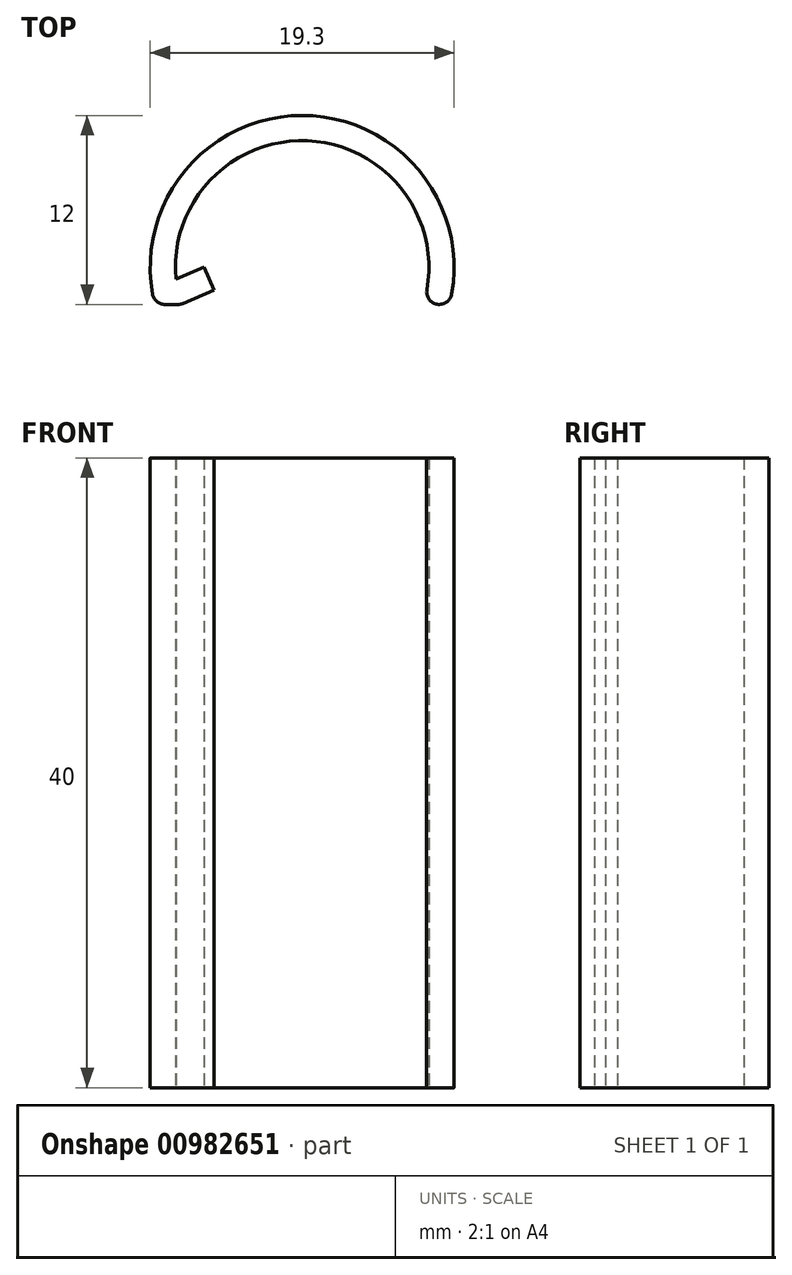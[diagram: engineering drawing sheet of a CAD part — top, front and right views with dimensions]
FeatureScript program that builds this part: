
annotation { "Feature Type Name" : "Feature", "Feature Type Description" : "" }
export const myFeature = defineFeature(function(context is Context, id is Id, definition is map)
    precondition{}
    {
        {
            var Q0;
            Q0=qCreatedBy(makeId("Top.planeOp"),FACE);
            var sketch = newSketch(context, id + "F0", { "sketchPlane" : qUnion([Q0])});
            skArc(sketch, "E0", {"start": v(7.7, -2.35) * mm, "mid": v(0.82, 8) * mm, "end": v(-8.02, -0.74) * mm});
            skArc(sketch, "E1.0", {"start": v(9.36, -2.35) * mm, "mid": v(0, 9.65) * mm, "end": v(-9.36, -2.35) * mm});
            skLineSegment(sketch, "E2", {"start": v(-6.2, 9.65) * mm, "end": v(12.66, 9.65) * mm, "construction": true});
            skArc(sketch, "E3.0", {"start": v(1.8, -0.14) * mm, "mid": v(0, 1.8) * mm, "end": v(-1.8, -0.14) * mm, "construction": true});
            skLineSegment(sketch, "E4", {"start": v(-7.7, -2.35) * mm, "end": v(-5.6, -1.44) * mm});
            skLineSegment(sketch, "E5.0", {"start": v(-8.02, -0.74) * mm, "end": v(-6.23, 0.03) * mm});
            skLineSegment(sketch, "E6.0", {"start": v(-9.36, -2.35) * mm, "end": v(-7.7, -2.35) * mm});
            skLineSegment(sketch, "E7.trimOffspring", {"start": v(7.7, -2.35) * mm, "end": v(9.36, -2.35) * mm});
            skLineSegment(sketch, "E8.0", {"start": v(-9.08, -2.95) * mm, "end": v(-9.72, -1.48) * mm, "construction": true});
            skLineSegment(sketch, "E9.0", {"start": v(-5.6, -1.44) * mm, "end": v(-6.23, 0.03) * mm});
            skSolve(sketch);
        }
        {
            var Q0;
            Q0=makeQuery(id+"F0.imprint","IMPRINT",FACE,{"disambiguationData":[TD([[makeQuery(id+"F0.imprint","IMPRINT",EDGE,{"derivedFrom":sQuery(id+"F0.wireOp",EDGE,"E0")}),-1.0]])]});
            extrude(context, id + "F1", {"entities" : qUnion([Q0]), "depth" : 40 * mm, "offsetDistance" : 25 * mm});
        }
        {
            var Q0;
            Q0=makeQuery(id+"F1.opExtrude","SWEPT_EDGE",EDGE,{"disambiguationData":[OSD([sQuery(id+"F0.wireOp",EDGE,"E1.0"),sQuery(id+"F0.wireOp",EDGE,"DFXZ1tWd-dZdo-E5LJ-Oaci-U77pfgr5Hmqq")])]});
            var Q1;
            Q1=makeQuery(id+"F1.opExtrude","SWEPT_EDGE",EDGE,{"disambiguationData":[OSD([sQuery(id+"F0.wireOp",EDGE,"E1.0"),sQuery(id+"F0.wireOp",EDGE,"11140bd1-0334-458a-a4ac-de3ad2aa48f0.trimOffspring")])]});
            var Q2;
            Q2=makeQuery(id+"F1.opExtrude","SWEPT_EDGE",EDGE,{"disambiguationData":[OSD([sQuery(id+"F0.wireOp",EDGE,"E4"),sQuery(id+"F0.wireOp",EDGE,"E6.0")])]});
            var Q3;
            Q3=makeQuery(id+"F1.opExtrude","SWEPT_EDGE",EDGE,{"disambiguationData":[OSD([sQuery(id+"F0.wireOp",EDGE,"E0"),sQuery(id+"F0.wireOp",EDGE,"E7.trimOffspring")])]});
            fillet(context, id + "F2", {"entities" : qUnion([Q0, Q1, Q2, Q3]), "radius" : 0.8 * mm, "tangentPropagation" : true, "allowEdgeOverflow" : false});
        }
    });
